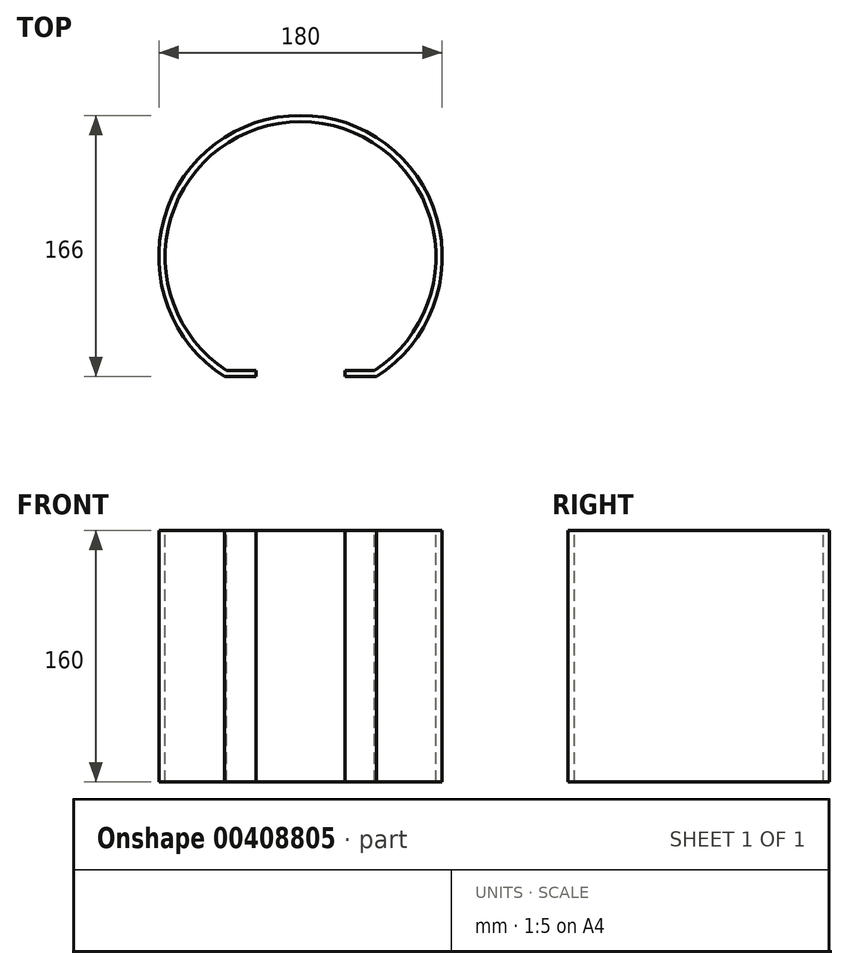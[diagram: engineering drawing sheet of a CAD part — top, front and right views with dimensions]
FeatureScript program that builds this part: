
annotation { "Feature Type Name" : "Feature", "Feature Type Description" : "" }
export const myFeature = defineFeature(function(context is Context, id is Id, definition is map)
    precondition{}
    {
        {
            var Q0;
            Q0=qCreatedBy(makeId("Top.planeOp"),FACE);
            var sketch = newSketch(context, id + "F0", { "sketchPlane" : qUnion([Q0])});
            skArc(sketch, "E0", {"start": v(48.2, -76) * mm, "mid": v(0, 90) * mm, "end": v(-48.2, -76) * mm});
            skLineSegment(sketch, "E1", {"start": v(-48.2, -76) * mm, "end": v(48.2, -76) * mm});
            skCircle(sketch, "E2", {"center": v(0, 0) * mm, "radius": 45 * mm, "construction": true});
            skSolve(sketch);
        }
        {
            var Q0;
            Q0=makeQuery(id+"F0.imprint","IMPRINT",FACE,{"disambiguationData":[TD([[makeQuery(id+"F0.imprint","IMPRINT",EDGE,{"derivedFrom":sQuery(id+"F0.wireOp",EDGE,"E0")}),1.0]])]});
            extrude(context, id + "F1", {"entities" : qUnion([Q0]), "depth" : 160 * mm});
        }
        {
            var Q0;
            Q0=makeQuery(id+"F1.opExtrude","CAP_FACE",FACE,{"disambiguationData":[OSD([sQuery(id+"F0.wireOp",EDGE,"E0"),sQuery(id+"F0.wireOp",EDGE,"E1")])],"isStart":false});
            var sketch = newSketch(context, id + "F2", { "sketchPlane" : qUnion([Q0])});
            skArc(sketch, "E3.0", {"start": v(47.03, -72) * mm, "mid": v(0, 86) * mm, "end": v(-47.03, -72) * mm});
            skLineSegment(sketch, "E3.1", {"start": v(-47.03, -72) * mm, "end": v(47.03, -72) * mm});
            skSolve(sketch);
        }
        {
            var Q0;
            Q0=makeQuery(id+"F2.imprint","IMPRINT",FACE,{"disambiguationData":[TD([[makeQuery(id+"F2.imprint","IMPRINT",EDGE,{"derivedFrom":sQuery(id+"F2.wireOp",EDGE,"E3.0")}),1.0]])]});
            extrude(context, id + "F3", {"entities" : qUnion([Q0]), "operationType" : NewBodyOperationType.REMOVE, "endBound" : BoundingType.UP_TO_NEXT, "oppositeDirection" : true, "depth" : 154 * mm});
        }
        {
            var Q0;
            Q0=makeQuery(id+"F1.opExtrude","SWEPT_FACE",FACE,{"disambiguationData":[OSD([sQuery(id+"F0.wireOp",EDGE,"E1")])]});
            var sketch = newSketch(context, id + "F4", { "sketchPlane" : qUnion([Q0])});
            skLineSegment(sketch, "E4.0", {"start": v(-28.2, 160) * mm, "end": v(-28.2, 0) * mm});
            skLineSegment(sketch, "E5.0", {"start": v(28.2, 160) * mm, "end": v(28.2, 0) * mm});
            skSolve(sketch);
        }
        {
            var Q0;
            Q0 = qSketchRegion(id + "F4", true);
            var Q1;
            {var subQ0=sQuery(id+"F4.wireOp",EDGE,"E4.0");Q1=makeQuery(id+"F4.imprint","IMPRINT",FACE,{"disambiguationData":[TD([[makeQuery(id+"F4.imprint","IMPRINT",EDGE,{"derivedFrom":subQ0}),1.0]])]});}
            extrude(context, id + "F5", {"entities" : qUnion([Q0, Q1]), "operationType" : NewBodyOperationType.REMOVE, "endBound" : BoundingType.UP_TO_NEXT, "oppositeDirection" : true, "depth" : 25 * mm});
        }
    });
